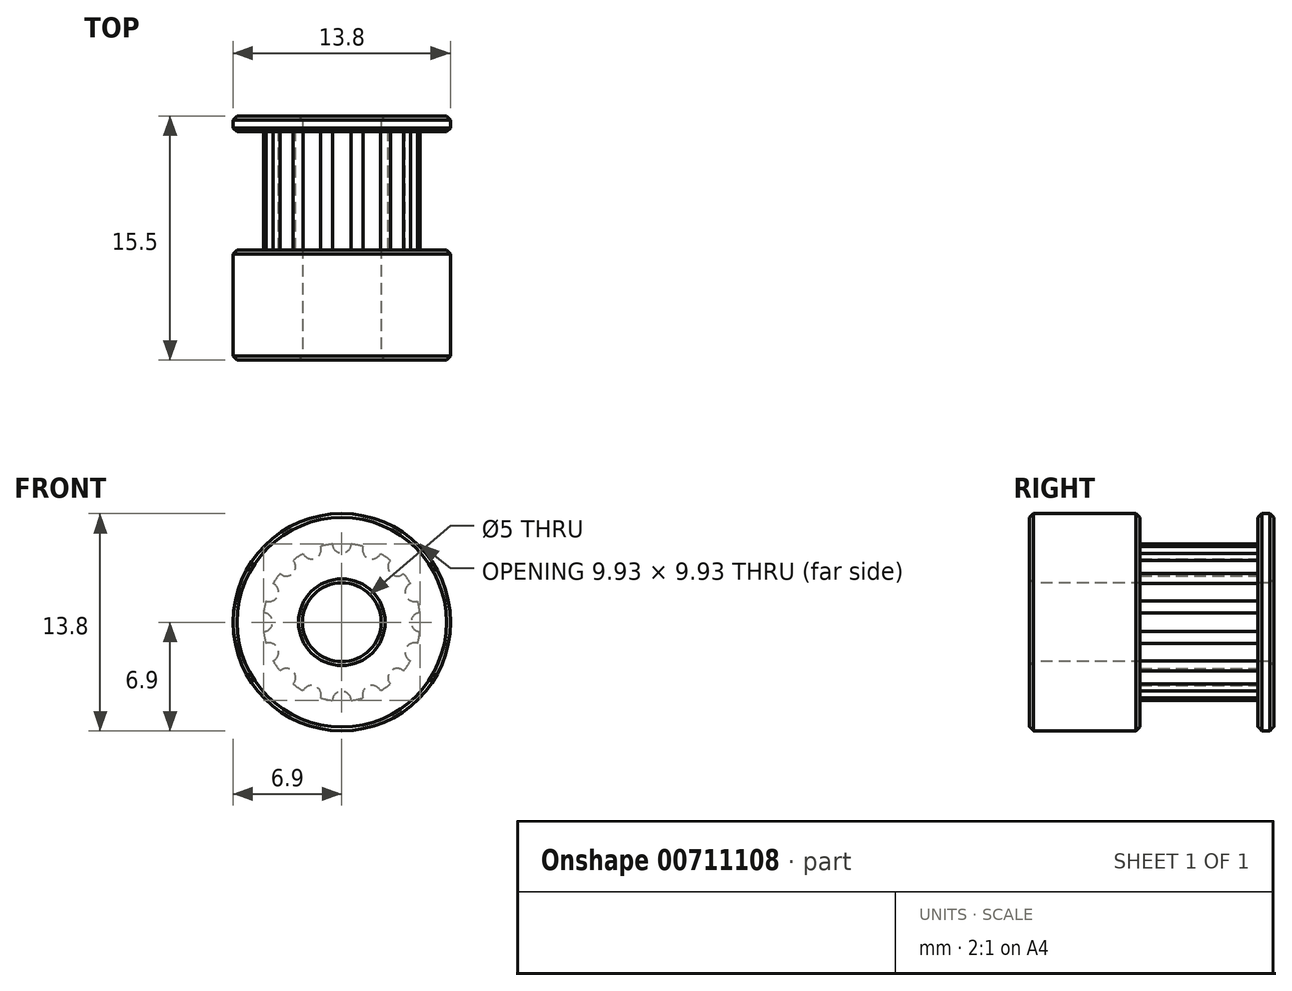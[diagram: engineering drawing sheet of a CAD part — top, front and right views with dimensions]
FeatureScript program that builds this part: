
annotation { "Feature Type Name" : "Feature", "Feature Type Description" : "" }
export const myFeature = defineFeature(function(context is Context, id is Id, definition is map)
    precondition{}
    {
        {
            var Q0;
            Q0=qCreatedBy(makeId("Front.planeOp"),FACE);
            var sketch = newSketch(context, id + "F0", { "sketchPlane" : qUnion([Q0])});
            skCircle(sketch, "E0", {"center": v(0, 0) * mm, "radius": 6.9 * mm});
            skSolve(sketch);
        }
        {
            var Q0;
            Q0=makeQuery(id+"F0.imprint","IMPRINT",FACE,{"disambiguationData":[TD([[makeQuery(id+"F0.imprint","IMPRINT",EDGE,{"derivedFrom":sQuery(id+"F0.wireOp",EDGE,"E0")}),1.0]])]});
            extrude(context, id + "F1", {"entities" : qUnion([Q0]), "depth" : 1 * mm, "offsetDistance" : 25 * mm});
        }
        {
            var Q0;
            Q0=makeQuery(id+"F1.opExtrude","CAP_FACE",FACE,{"disambiguationData":[OSD([sQuery(id+"F0.wireOp",EDGE,"E0")])],"isStart":false});
            var sketch = newSketch(context, id + "F2", { "sketchPlane" : qUnion([Q0])});
            skCircle(sketch, "E1", {"center": v(0, 0) * mm, "radius": 5 * mm});
            skSolve(sketch);
        }
        {
            var Q0;
            Q0 = qSketchRegion(id + "F2", true);
            extrude(context, id + "F3", {"entities" : qUnion([Q0]), "operationType" : NewBodyOperationType.ADD, "depth" : 7.5 * mm, "offsetDistance" : 25 * mm});
        }
        {
            var Q0;
            Q0=makeQuery(id+"F3.opExtrude","CAP_FACE",FACE,{"disambiguationData":[OSD([sQuery(id+"F2.wireOp",EDGE,"E1")])],"isStart":false});
            var sketch = newSketch(context, id + "F4", { "sketchPlane" : qUnion([Q0])});
            skCircle(sketch, "E2", {"center": v(0, 0) * mm, "radius": 6.9 * mm});
            skSolve(sketch);
        }
        {
            var Q0;
            Q0 = qSketchRegion(id + "F4", true);
            extrude(context, id + "F5", {"entities" : qUnion([Q0]), "operationType" : NewBodyOperationType.ADD, "depth" : 7 * mm, "offsetDistance" : 25 * mm});
        }
        {
            var Q0;
            Q0=makeQuery(id+"F1.opExtrude","CAP_FACE",FACE,{"disambiguationData":[OSD([sQuery(id+"F0.wireOp",EDGE,"E0")])],"isStart":false});
            var sketch = newSketch(context, id + "F6", { "sketchPlane" : qUnion([Q0])});
            skCircle(sketch, "E3", {"center": v(0, 0) * mm, "radius": 5 * mm, "construction": true});
            skLineSegment(sketch, "E4", {"start": v(-5, 0) * mm, "end": v(0, 0) * mm, "construction": true});
            skLineSegment(sketch, "E5", {"start": v(0, 0) * mm, "end": v(0, 5) * mm, "construction": true});
            skCircle(sketch, "E6", {"center": v(0, 5) * mm, "radius": 0.6 * mm});
            skCircle(sketch, "E7.1.0", {"center": v(-1.91, 4.62) * mm, "radius": 0.6 * mm});
            skCircle(sketch, "E7.2.0", {"center": v(-3.54, 3.54) * mm, "radius": 0.6 * mm});
            skCircle(sketch, "E7.3.0", {"center": v(-4.62, 1.91) * mm, "radius": 0.6 * mm});
            skCircle(sketch, "E7.4.0", {"center": v(-5, 0) * mm, "radius": 0.6 * mm});
            skCircle(sketch, "E7.5.0", {"center": v(-4.62, -1.91) * mm, "radius": 0.6 * mm});
            skCircle(sketch, "E7.6.0", {"center": v(-3.54, -3.54) * mm, "radius": 0.6 * mm});
            skCircle(sketch, "E7.7.0", {"center": v(-1.91, -4.62) * mm, "radius": 0.6 * mm});
            skCircle(sketch, "E7.8.0", {"center": v(0, -5) * mm, "radius": 0.6 * mm});
            skCircle(sketch, "E7.9.0", {"center": v(1.91, -4.62) * mm, "radius": 0.6 * mm});
            skCircle(sketch, "E7.10.0", {"center": v(3.54, -3.54) * mm, "radius": 0.6 * mm});
            skCircle(sketch, "E7.11.0", {"center": v(4.62, -1.91) * mm, "radius": 0.6 * mm});
            skCircle(sketch, "E7.12.0", {"center": v(5, 0) * mm, "radius": 0.6 * mm});
            skCircle(sketch, "E7.13.0", {"center": v(4.62, 1.91) * mm, "radius": 0.6 * mm});
            skCircle(sketch, "E7.14.0", {"center": v(3.54, 3.54) * mm, "radius": 0.6 * mm});
            skCircle(sketch, "E7.15.0", {"center": v(1.91, 4.62) * mm, "radius": 0.6 * mm});
            skSolve(sketch);
        }
        {
            var Q0;
            Q0 = qSketchRegion(id + "F6", true);
            var Q1;
            Q1=makeQuery(id+"F5.opExtrude","CAP_FACE",FACE,{"disambiguationData":[OSD([sQuery(id+"F4.wireOp",EDGE,"E2")])],"isStart":true});
            extrude(context, id + "F7", {"entities" : qUnion([Q0]), "operationType" : NewBodyOperationType.REMOVE, "endBound" : BoundingType.UP_TO_SURFACE, "depth" : 7.5 * mm, "endBoundEntityFace" : qUnion([Q1]), "offsetDistance" : 25 * mm});
        }
        {
            var Q0;
            Q0=makeQuery(id+"F5.opExtrude","CAP_FACE",FACE,{"disambiguationData":[OSD([sQuery(id+"F4.wireOp",EDGE,"E2")])],"isStart":false});
            var sketch = newSketch(context, id + "F8", { "sketchPlane" : qUnion([Q0])});
            skCircle(sketch, "E8", {"center": v(0, 0) * mm, "radius": 2.5 * mm});
            skSolve(sketch);
        }
        {
            var Q0;
            Q0 = qSketchRegion(id + "F8", true);
            extrude(context, id + "F9", {"entities" : qUnion([Q0]), "operationType" : NewBodyOperationType.REMOVE, "endBound" : BoundingType.THROUGH_ALL, "oppositeDirection" : true, "depth" : 25 * mm, "offsetDistance" : 25 * mm});
        }
        {
            var Q0;
            Q0=makeQuery(id+"F5.opExtrude","SWEPT_FACE",FACE,{"disambiguationData":[OSD([sQuery(id+"F4.wireOp",EDGE,"E2")])]});
            var Q1;
            Q1=makeQuery(id+"F1.opExtrude","SWEPT_FACE",FACE,{"disambiguationData":[OSD([sQuery(id+"F0.wireOp",EDGE,"E0")])]});
            var Q2;
            Q2=makeQuery(id+"F9.boolean.opBoolean","COPY",FACE,{"derivedFrom":makeQuery(id+"F9.opExtrude","SWEPT_FACE",FACE,{"disambiguationData":[OSD([sQuery(id+"F8.wireOp",EDGE,"E8")])]})});
            chamfer(context, id + "F10", {"entities" : qUnion([Q0, Q1, Q2]), "width" : 0.25 * mm, "tangentPropagation" : true});
        }
    });
